# Revit family: 6L-R-D
name_source: partatom
category: Lighting Fixtures
units: mm (PartAtom-declared; Revit-internal decimal feet)

## family parameters
Cut with Voids When Loaded = No
Host = Face
Light Source = Yes
OmniClass Number = 23.80.70.11
OmniClass Title = Luminaries for Internal Lighting
Part Type = Normal
Room Calculation Point = No
Round Connector Dimension = Use Diameter
Shared = No

## types (1)
- 6L-R-D
    Apparent Load = 0 VA
    Circuiting = 1 Circuit
    Color Filter = 16777215
    Default Elevation = 48 "
    Description = MOD 6 LED Recessed Slot
    Dimming = D10
    Dimming Lamp Color Temperature Shift = <None>
    Distribution = Direct
    Emit Shape Visible in Rendering = No
    Emit from Rectangle Length = 22 "
    Emit from Rectangle Width = 6.5 "
    Lamp = LED Lamp
    Length = 24 "
    Load Classification = Lighting
    Manufacturer = Litecontrol
    Material Finish = Paint - Matte White
    Model = 6L-R-D
    Opal lens = Glass
    Photometric Web File = generic
    Power factor = 1
    Tilt Angle = -90.00°
    URL = https://www.currentlighting.com
    Voltage = 120 V
    Wattage Comments = 5-10W
    Watts = 5 W
    zzLength1 = 8.438 "

## geometry (parser evidence)
native form markers: Sweep x5
no freeform markers — native parametric forms only
